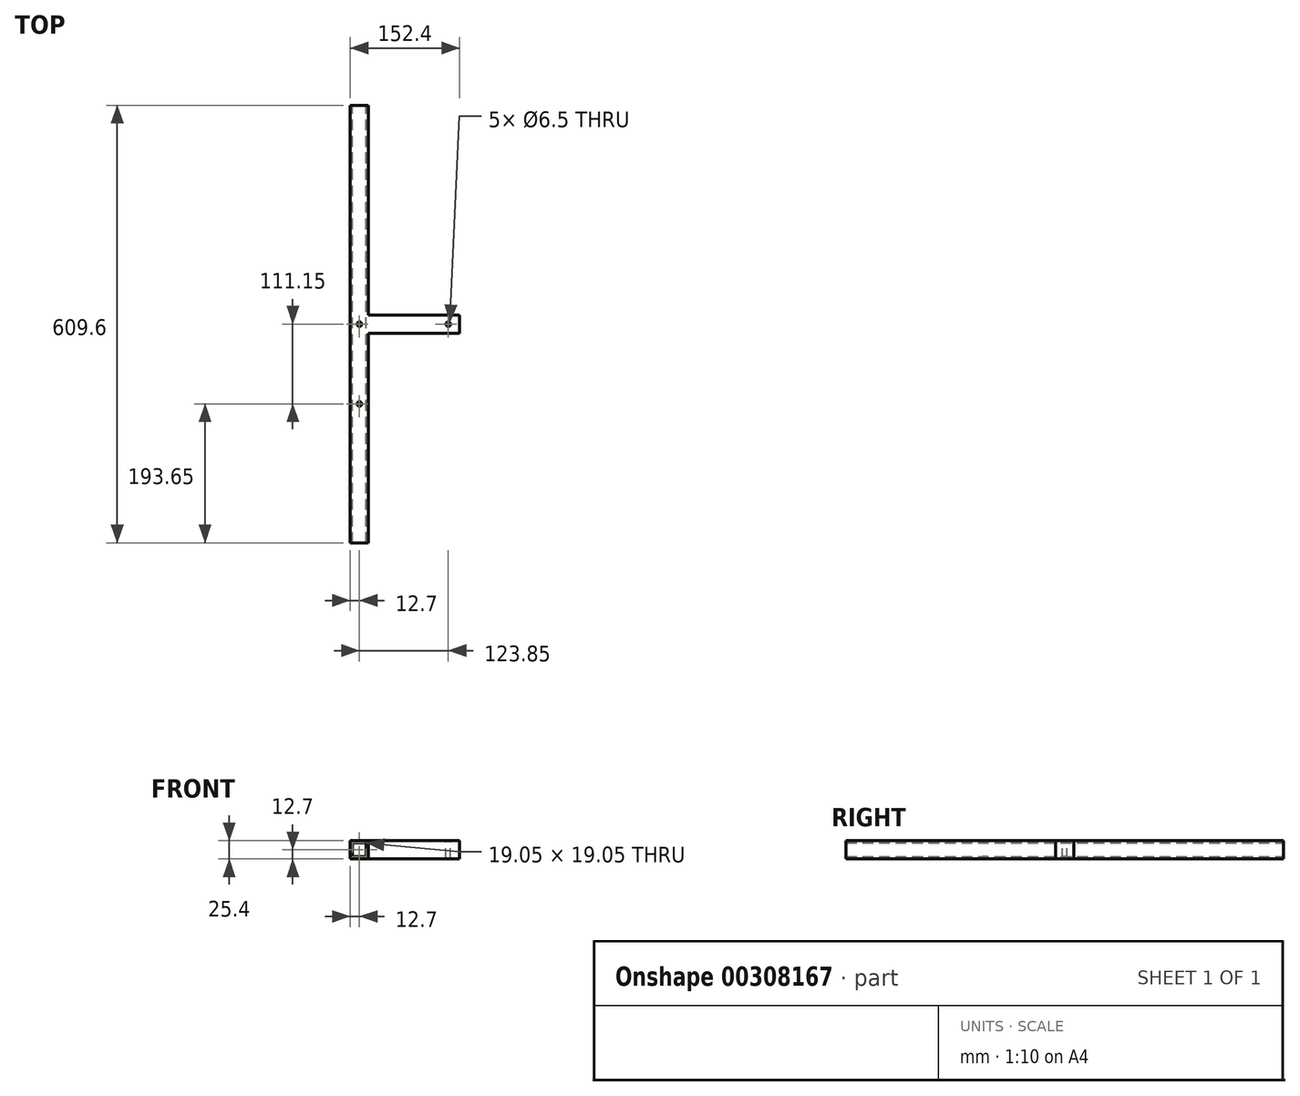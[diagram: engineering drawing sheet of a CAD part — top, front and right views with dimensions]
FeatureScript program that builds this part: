
annotation { "Feature Type Name" : "Feature", "Feature Type Description" : "" }
export const myFeature = defineFeature(function(context is Context, id is Id, definition is map)
    precondition{}
    {
        {
            var Q0;
            Q0=qCreatedBy(makeId("Front.planeOp"),FACE);
            var sketch = newSketch(context, id + "F0", { "sketchPlane" : qUnion([Q0])});
            skLineSegment(sketch, "E0.bottom", {"start": v(12.7, 12.7) * mm, "end": v(-12.7, 12.7) * mm});
            skLineSegment(sketch, "E0.top", {"start": v(12.7, -12.7) * mm, "end": v(-12.7, -12.7) * mm});
            skLineSegment(sketch, "E0.left", {"start": v(12.7, 12.7) * mm, "end": v(12.7, -12.7) * mm});
            skLineSegment(sketch, "E0.right", {"start": v(-12.7, 12.7) * mm, "end": v(-12.7, -12.7) * mm});
            skPoint(sketch, "E0.middle", {"position": v(0, 0) * mm});
            skLineSegment(sketch, "E1.bottom", {"start": v(9.52, 9.53) * mm, "end": v(-9.53, 9.52) * mm});
            skLineSegment(sketch, "E1.top", {"start": v(9.53, -9.53) * mm, "end": v(-9.52, -9.53) * mm});
            skLineSegment(sketch, "E1.left", {"start": v(9.52, 9.53) * mm, "end": v(9.53, -9.52) * mm});
            skLineSegment(sketch, "E1.right", {"start": v(-9.53, 9.52) * mm, "end": v(-9.52, -9.53) * mm});
            skLineSegment(sketch, "E2", {"start": v(-12.7, -12.7) * mm, "end": v(-9.52, -9.53) * mm, "construction": true});
            skLineSegment(sketch, "E3", {"start": v(9.53, -9.52) * mm, "end": v(12.7, -12.7) * mm, "construction": true});
            skSolve(sketch);
        }
        {
            var Q0;
            Q0 = qSketchRegion(id + "F0", true);
            extrude(context, id + "F1", {"entities" : qUnion([Q0]), "endBound" : BoundingType.SYMMETRIC, "depth" : 609.6 * mm});
        }
        {
            var Q0;
            Q0=makeQuery(id+"F1.opExtrude","SWEPT_FACE",FACE,{"disambiguationData":[OSD([sQuery(id+"F0.wireOp",EDGE,"E0.left")])]});
            var sketch = newSketch(context, id + "F2", { "sketchPlane" : qUnion([Q0])});
            skLineSegment(sketch, "E4.bottom", {"start": v(12.7, 12.7) * mm, "end": v(-12.7, 12.7) * mm});
            skLineSegment(sketch, "E4.top", {"start": v(12.7, -12.7) * mm, "end": v(-12.7, -12.7) * mm});
            skLineSegment(sketch, "E4.left", {"start": v(12.7, 12.7) * mm, "end": v(12.7, -12.7) * mm});
            skLineSegment(sketch, "E4.right", {"start": v(-12.7, 12.7) * mm, "end": v(-12.7, -12.7) * mm});
            skPoint(sketch, "E4.middle", {"position": v(0, 0) * mm});
            skSolve(sketch);
        }
        {
            var Q0;
            Q0 = qSketchRegion(id + "F2", true);
            extrude(context, id + "F3", {"entities" : qUnion([Q0]), "operationType" : NewBodyOperationType.ADD, "depth" : 127 * mm});
        }
        {
            var Q0;
            Q0=makeQuery(id+"F3.boolean.opBoolean","MERGE",FACE,{"derivedFrom":[makeQuery(id+"F1.opExtrude","SWEPT_FACE",FACE,{"disambiguationData":[OSD([sQuery(id+"F0.wireOp",EDGE,"E0.bottom")])]}),makeQuery(id+"F3.opExtrude","SWEPT_FACE",FACE,{"disambiguationData":[OSD([sQuery(id+"F2.wireOp",EDGE,"E4.bottom")])]})]});
            var sketch = newSketch(context, id + "F4", { "sketchPlane" : qUnion([Q0])});
            skLineSegment(sketch, "E5.bottom", {"start": v(0, 0) * mm, "end": v(123.85, 0) * mm, "construction": true});
            skLineSegment(sketch, "E5.top", {"start": v(0, -111.15) * mm, "end": v(123.85, -111.15) * mm, "construction": true});
            skLineSegment(sketch, "E5.left", {"start": v(0, 0) * mm, "end": v(0, -111.15) * mm, "construction": true});
            skLineSegment(sketch, "E5.right", {"start": v(123.85, 0) * mm, "end": v(123.85, -111.15) * mm, "construction": true});
            skCircle(sketch, "E6", {"center": v(0, 0) * mm, "radius": 3.25 * mm});
            skCircle(sketch, "E7", {"center": v(123.85, 0) * mm, "radius": 3.25 * mm});
            skCircle(sketch, "E8", {"center": v(123.85, -111.15) * mm, "radius": 3.25 * mm, "construction": true});
            skCircle(sketch, "E9", {"center": v(0, -111.15) * mm, "radius": 3.25 * mm});
            skSolve(sketch);
        }
        {
            var Q0;
            Q0 = qSketchRegion(id + "F4", true);
            extrude(context, id + "F5", {"entities" : qUnion([Q0]), "operationType" : NewBodyOperationType.REMOVE, "endBound" : BoundingType.THROUGH_ALL, "oppositeDirection" : true, "depth" : 25.4 * mm});
        }
    });
